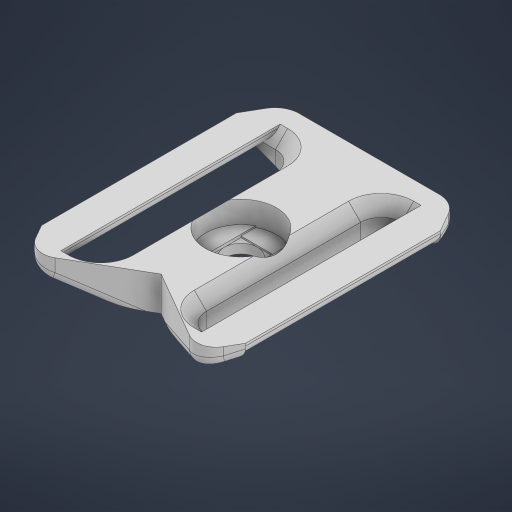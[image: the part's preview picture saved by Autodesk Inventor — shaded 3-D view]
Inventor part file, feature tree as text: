
AUTODESK INVENTOR PART (.ipt)
format: ipt  version: 2023 (Build 270158000, 158)  size: 508,416 bytes
history: native  units: in
note: dims shown in document units (in); Inventor stores cm internally (conversion verified against a paired STEP export)
features: extrude x8, sketch x5, chamfer x4, direct_edit x3, fillet x3, move_body x3
ambient origin geometry x8: Origin, YZ Plane, XZ Plane, XY Plane, X Axis, Y Axis, Z Axis, Center Point
bodies: Solid1 (feature_tree)
feature tree (26):
  sketch  "Sketch1"  dims[d2=0.1181in d3=0.0in d5=0.2677in]
  extrude  "Extrusion1"  Depth=0.1181in
  extrude  "Extrusion5"  Depth=0.785in
  extrude  "Extrusion7"  Depth=0.0591in
  direct_edit  "Direct Edit2"
  extrude  "Extrusion8"  Depth=0.315in
  direct_edit  "Direct Edit3"
  sketch  "Sketch8"  dims[d12=0.7874in d18=0.315in]
  extrude  "Extrusion9"  Depth=0.0787in
  extrude  "Extrusion10"  Depth=0.1969in
  chamfer  "Chamfer2"  Distance=0.1575in
  fillet  "Fillet1"  Radius=0.3051in
  extrude  "Extrusion11"  Depth=0.0787in
  chamfer  "Chamfer4"  [1 undecoded]
  chamfer  "Chamfer3"  [1 undecoded]
  fillet  "Fillet2"  Radius=0.0591in
  fillet  "Fillet3"  [1 undecoded]
  direct_edit  "Direct Edit4"
  extrude  "Extrusion13"  TaperAngle=0.0deg  [1 undecoded]
  chamfer  "Chamfer5"  Distance=0.0591in
  sketch  "Sketch6"  dims[d6=2.2146in d7=0.785in]
  sketch  "Sketch7"  dims[d8=0.5709in d9=0.0591in]
  sketch  "Sketch10"  dims[d20=0.1575in d21=0.1575in d27=0.1969in d30=0.1575in d31=0.0in d37=0.3051in d38=0.3051in d44=0.0in d45=0.0in d46=0.0in d47=0.0in d48=-0.0591in d49=0.0591in d50=0.0in d51=0.0in d52=0.0in d53=0.0in d54=-0.0197in d55=0.0591in d56=0.0591in d57=0.0118in d58=0.0in d59=0.0236in d60=0.0in d61=0.0984in d62=0.0787in d63=45.0deg d64=0.0787in d65=0.2126in d67=0.1181in d68=0.3543in d69=0.0in d70=0.1884in d71=0.0787in d72=45.0deg d73=0.0492in d74=0.0787in d75=45.0deg d76=0.0787in d77=0.1181in d79=0.0394in d80=0.0in d81=-0.0394in d82=0.0in d86=0.1181in d87=0.0591in d88=0.0in d89=0.0591in d90=0.0787in d91=45.0deg d26=0.0197in d28=0.0197in d29=0.0344in d41=0.0197in d42=0.0344in d43=0.0197in]
  move_body  "Move2"
  move_body  "Move3"
  move_body  "Move4"
note: 4 required parameter values undecoded (feature->parameter linkage not recoverable at this tier; creation-order binding heuristic only, values carry confidence <= 0.55)
